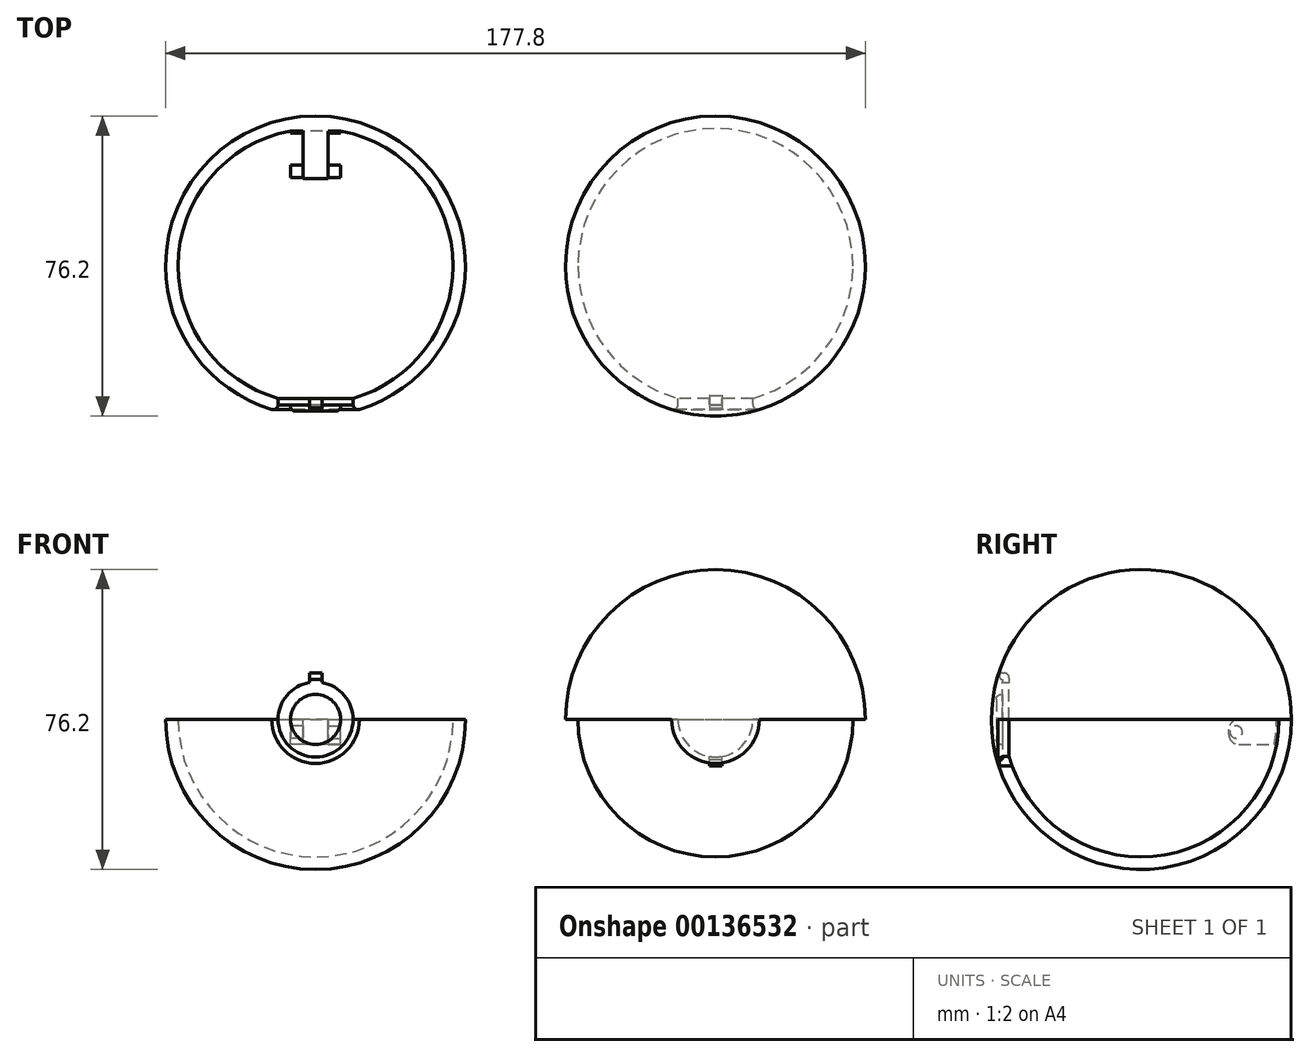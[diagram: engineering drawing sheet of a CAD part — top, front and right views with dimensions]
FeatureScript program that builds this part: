
annotation { "Feature Type Name" : "Feature", "Feature Type Description" : "" }
export const myFeature = defineFeature(function(context is Context, id is Id, definition is map)
    precondition{}
    {
        {
            var Q0;
            Q0=qCreatedBy(makeId("Top.planeOp"),FACE);
            var sketch = newSketch(context, id + "F0", { "sketchPlane" : qUnion([Q0])});
            skLineSegment(sketch, "E0", {"start": v(0, 0) * mm, "end": v(-50.8, 0) * mm});
            skCircle(sketch, "E1", {"center": v(-50.8, 0) * mm, "radius": 38.1 * mm});
            skLineSegment(sketch, "E2", {"start": v(0, 0) * mm, "end": v(50.8, 0) * mm});
            skCircle(sketch, "E3", {"center": v(50.8, 0) * mm, "radius": 38.1 * mm});
            skLineSegment(sketch, "E4", {"start": v(-50.8, 0) * mm, "end": v(-88.9, 0) * mm});
            skLineSegment(sketch, "E5", {"start": v(50.8, 0) * mm, "end": v(88.9, 0) * mm});
            skSolve(sketch);
        }
        {
            var Q0;
            {var subQ3=sQuery(id+"F0.wireOp",EDGE,"E4");Q0=makeQuery(id+"F0.imprint","IMPRINT",FACE,{"disambiguationData":[TD([[makeQuery(id+"F0.imprint","IMPRINT",EDGE,{"derivedFrom":subQ3}),1.0]])]});}
            var Q1;
            {var subQ3=sQuery(id+"F0.wireOp",EDGE,"E5");Q1=makeQuery(id+"F0.imprint","IMPRINT",FACE,{"disambiguationData":[TD([[makeQuery(id+"F0.imprint","IMPRINT",EDGE,{"derivedFrom":subQ3}),-1.0]])]});}
            var Q2;
            Q2=sQuery(id+"F0.wireOp",EDGE,"E0");
            revolve(context, id + "F1", {"surfaceOperationType" : NewSurfaceOperationType.NEW, "entities" : qUnion([Q0, Q1]), "axis" : qUnion([Q2]), "revolveType" : RevolveType.ONE_DIRECTION, "oppositeDirection" : true, "angle" : 180 * degree});
        }
        {
            var Q0;
            Q0=makeQuery(id+"F1.opRevolve","CAP_FACE",FACE,{"disambiguationData":[OSD([sQuery(id+"F0.wireOp",EDGE,"E0"),sQuery(id+"F0.wireOp",EDGE,"E1"),sQuery(id+"F0.wireOp",EDGE,"E4")])],"isStart":false});
            var sketch = newSketch(context, id + "F2", { "sketchPlane" : qUnion([Q0])});
            skCircle(sketch, "E6", {"center": v(-50.8, 0) * mm, "radius": 34.93 * mm});
            skLineSegment(sketch, "E7", {"start": v(-15.88, 0) * mm, "end": v(-85.73, 0) * mm});
            skSolve(sketch);
        }
        {
            var Q0;
            {var subQ0=sQuery(id+"F2.wireOp",EDGE,"E7");Q0=makeQuery(id+"F2.imprint","IMPRINT",FACE,{"disambiguationData":[TD([[makeQuery(id+"F2.imprint","IMPRINT",EDGE,{"derivedFrom":subQ0}),1.0]])]});}
            var Q1;
            Q1=sQuery(id+"F2.wireOp",EDGE,"E7");
            revolve(context, id + "F3", {"operationType" : NewBodyOperationType.REMOVE, "surfaceOperationType" : NewSurfaceOperationType.NEW, "entities" : qUnion([Q0]), "axis" : qUnion([Q1]), "revolveType" : RevolveType.FULL, "oppositeDirection" : true});
        }
        {
            var Q0;
            Q0=makeQuery(id+"F1.opRevolve","CAP_FACE",FACE,{"disambiguationData":[OSD([sQuery(id+"F0.wireOp",EDGE,"E2"),sQuery(id+"F0.wireOp",EDGE,"E3"),sQuery(id+"F0.wireOp",EDGE,"E5")])],"isStart":false});
            var sketch = newSketch(context, id + "F4", { "sketchPlane" : qUnion([Q0])});
            skCircle(sketch, "E8", {"center": v(50.8, 0) * mm, "radius": 34.93 * mm});
            skLineSegment(sketch, "E9", {"start": v(15.88, 0) * mm, "end": v(85.73, 0) * mm});
            skSolve(sketch);
        }
        {
            var Q0;
            {var subQ0=sQuery(id+"F4.wireOp",EDGE,"E9");Q0=makeQuery(id+"F4.imprint","IMPRINT",FACE,{"disambiguationData":[TD([[makeQuery(id+"F4.imprint","IMPRINT",EDGE,{"derivedFrom":subQ0}),-1.0]])]});}
            var Q1;
            Q1=sQuery(id+"F4.wireOp",EDGE,"E9");
            revolve(context, id + "F5", {"operationType" : NewBodyOperationType.REMOVE, "surfaceOperationType" : NewSurfaceOperationType.NEW, "entities" : qUnion([Q0]), "axis" : qUnion([Q1]), "revolveType" : RevolveType.FULL, "oppositeDirection" : true});
        }
        {
            var Q0;
            Q0=qCreatedBy(makeId("Front.planeOp"),FACE);
            var sketch = newSketch(context, id + "F6", { "sketchPlane" : qUnion([Q0])});
            skLineSegment(sketch, "E10", {"start": v(0, 0) * mm, "end": v(-50.8, 0) * mm});
            skCircle(sketch, "E11", {"center": v(-50.8, 0) * mm, "radius": 9.53 * mm});
            skSolve(sketch);
        }
        {
            var Q0;
            Q0 = qSketchRegion(id + "F6", true);
            extrude(context, id + "F7", {"entities" : qUnion([Q0]), "operationType" : NewBodyOperationType.REMOVE, "depth" : 50.8 * mm, "offsetDistance" : 25.4 * mm});
        }
        {
            var Q0;
            Q0=makeQuery(id+"F1.opRevolve","CAP_FACE",FACE,{"disambiguationData":[OSD([sQuery(id+"F0.wireOp",EDGE,"E0"),sQuery(id+"F0.wireOp",EDGE,"E1"),sQuery(id+"F0.wireOp",EDGE,"E4")])],"isStart":false});
            var sketch = newSketch(context, id + "F8", { "sketchPlane" : qUnion([Q0])});
            skLineSegment(sketch, "E12", {"start": v(-60.32, -33.6) * mm, "end": v(-41.28, -33.6) * mm});
            skLineSegment(sketch, "E13", {"start": v(-41.28, -33.6) * mm, "end": v(-41.28, -36.9) * mm});
            skLineSegment(sketch, "E14", {"start": v(-41.28, -36.9) * mm, "end": v(-60.33, -36.9) * mm});
            skLineSegment(sketch, "E15", {"start": v(-60.33, -36.9) * mm, "end": v(-60.33, -33.6) * mm});
            skLineSegment(sketch, "E16", {"start": v(-60.33, -33.6) * mm, "end": v(-60.33, -35.25) * mm});
            skLineSegment(sketch, "E17", {"start": v(-60.33, -35.25) * mm, "end": v(-41.28, -35.25) * mm});
            skLineSegment(sketch, "E18", {"start": v(-50.8, -33.6) * mm, "end": v(-50.8, -36.9) * mm});
            skLineSegment(sketch, "E19", {"start": v(-60.33, -35.25) * mm, "end": v(-57.15, -35.25) * mm});
            skLineSegment(sketch, "E20", {"start": v(-57.15, -35.25) * mm, "end": v(-57.15, -36.9) * mm});
            skSolve(sketch);
        }
        {
            var Q0;
            {var subQ0=sQuery(id+"F8.wireOp",EDGE,"E18");var subQ1=sQuery(id+"F8.wireOp",EDGE,"E17");var subQ2=makeQuery(id+"F8.imprint","INTERSECT",VERTEX,{"derivedFrom":[subQ1,subQ0]});Q0=makeQuery(id+"F8.imprint","IMPRINT",FACE,{"disambiguationData":[TD([[makeQuery(id+"F8.imprint","IMPRINT",EDGE,{"disambiguationData":[TD([[subQ2,1.0]])],"derivedFrom":subQ1}),1.0]])]});}
            var Q1;
            {var subQ3=sQuery(id+"F8.wireOp",EDGE,"E20");Q1=makeQuery(id+"F8.imprint","IMPRINT",FACE,{"disambiguationData":[TD([[makeQuery(id+"F8.imprint","IMPRINT",EDGE,{"derivedFrom":subQ3}),1.0]])]});}
            var Q2;
            Q2=sQuery(id+"F8.wireOp",EDGE,"E18");
            revolve(context, id + "F9", {"operationType" : NewBodyOperationType.ADD, "surfaceOperationType" : NewSurfaceOperationType.NEW, "entities" : qUnion([Q0, Q1]), "axis" : qUnion([Q2]), "revolveType" : RevolveType.FULL});
        }
        {
            var Q0;
            Q0=qCreatedBy(makeId("Front.planeOp"),FACE);
            var sketch = newSketch(context, id + "F10", { "sketchPlane" : qUnion([Q0])});
            skLineSegment(sketch, "E21", {"start": v(0, 0) * mm, "end": v(50.8, 0) * mm});
            skCircle(sketch, "E22", {"center": v(50.8, 0) * mm, "radius": 9.53 * mm});
            skSolve(sketch);
        }
        {
            var Q0;
            Q0 = qSketchRegion(id + "F10", true);
            extrude(context, id + "F11", {"entities" : qUnion([Q0]), "operationType" : NewBodyOperationType.REMOVE, "depth" : 50.8 * mm, "offsetDistance" : 25.4 * mm});
        }
        {
            var Q0;
            Q0=makeQuery(id+"F9.opRevolve","SWEPT_EDGE",EDGE,{"disambiguationData":[OSD([sQuery(id+"F8.wireOp",EDGE,"E14"),sQuery(id+"F8.wireOp",EDGE,"E20")])]});
            var Q1;
            Q1=makeQuery(id+"F7.boolean.opBoolean","INTERSECT",EDGE,{"derivedFrom":[makeQuery(id+"F1.opRevolve","SWEPT_FACE",FACE,{"disambiguationData":[OSD([sQuery(id+"F0.wireOp",EDGE,"E1")])]}),makeQuery(id+"F7.opExtrude","SWEPT_FACE",FACE,{"disambiguationData":[OSD([sQuery(id+"F6.wireOp",EDGE,"E11")])]})]});
            var Q2;
            Q2=makeQuery(id+"F11.boolean.opBoolean","INTERSECT",EDGE,{"derivedFrom":[makeQuery(id+"F1.opRevolve","SWEPT_FACE",FACE,{"disambiguationData":[OSD([sQuery(id+"F0.wireOp",EDGE,"E3")])]}),makeQuery(id+"F11.opExtrude","SWEPT_FACE",FACE,{"disambiguationData":[OSD([sQuery(id+"F10.wireOp",EDGE,"E22")])]})]});
            fillet(context, id + "F12", {"entities" : qUnion([Q0, Q1, Q2]), "tangentPropagation" : true, "radius" : 1.27 * mm, "defaultsChanged" : false, "vertexSettings" : [], "allowEdgeOverflow" : false});
        }
        {
            var Q0;
            Q0=makeQuery(id+"F1.opRevolve","CAP_FACE",FACE,{"disambiguationData":[OSD([sQuery(id+"F0.wireOp",EDGE,"E2"),sQuery(id+"F0.wireOp",EDGE,"E3"),sQuery(id+"F0.wireOp",EDGE,"E5")])],"isStart":false});
            var sketch = newSketch(context, id + "F13", { "sketchPlane" : qUnion([Q0])});
            skLineSegment(sketch, "E23", {"start": v(60.32, -33.6) * mm, "end": v(41.28, -33.6) * mm});
            skLineSegment(sketch, "E24", {"start": v(50.8, -33.6) * mm, "end": v(52.39, -33.6) * mm});
            skLineSegment(sketch, "E25", {"start": v(50.8, -33.6) * mm, "end": v(49.21, -33.6) * mm});
            skLineSegment(sketch, "E26", {"start": v(52.39, -33.6) * mm, "end": v(52.39, -35.25) * mm});
            skLineSegment(sketch, "E27", {"start": v(49.21, -33.6) * mm, "end": v(49.21, -35.25) * mm});
            skLineSegment(sketch, "E28", {"start": v(50.8, -33.6) * mm, "end": v(50.8, -35.25) * mm});
            skLineSegment(sketch, "E29", {"start": v(50.8, -35.25) * mm, "end": v(52.39, -35.25) * mm});
            skLineSegment(sketch, "E30", {"start": v(50.8, -35.25) * mm, "end": v(49.21, -35.25) * mm});
            skLineSegment(sketch, "E31", {"start": v(52.39, -33.6) * mm, "end": v(52.39, -33.1) * mm});
            skLineSegment(sketch, "E32", {"start": v(52.39, -33.1) * mm, "end": v(49.21, -33.1) * mm});
            skLineSegment(sketch, "E33", {"start": v(49.21, -33.1) * mm, "end": v(49.21, -33.6) * mm});
            skSolve(sketch);
        }
        {
            var Q0;
            {var subQ2=sQuery(id+"F13.wireOp",EDGE,"E26");Q0=makeQuery(id+"F13.imprint","IMPRINT",FACE,{"disambiguationData":[TD([[makeQuery(id+"F13.imprint","IMPRINT",EDGE,{"derivedFrom":subQ2}),-1.0]])]});}
            var Q1;
            {var subQ0=sQuery(id+"F13.wireOp",EDGE,"E27");Q1=makeQuery(id+"F13.imprint","IMPRINT",FACE,{"disambiguationData":[TD([[makeQuery(id+"F13.imprint","IMPRINT",EDGE,{"derivedFrom":subQ0}),1.0]])]});}
            var Q2;
            {var subQ0=sQuery(id+"F13.wireOp",EDGE,"E31");Q2=makeQuery(id+"F13.imprint","IMPRINT",FACE,{"disambiguationData":[TD([[makeQuery(id+"F13.imprint","IMPRINT",EDGE,{"derivedFrom":subQ0}),1.0]])]});}
            extrude(context, id + "F14", {"entities" : qUnion([Q0, Q1, Q2]), "operationType" : NewBodyOperationType.REMOVE, "oppositeDirection" : true, "depth" : 10.16 * mm, "offsetDistance" : 25.4 * mm});
        }
        {
            var Q0;
            Q0=makeQuery(id+"F9.opRevolve","SWEPT_FACE",FACE,{"disambiguationData":[OSD([sQuery(id+"F8.wireOp",EDGE,"E12")])]});
            var sketch = newSketch(context, id + "F15", { "sketchPlane" : qUnion([Q0])});
            skLineSegment(sketch, "E34", {"start": v(50.8, 0) * mm, "end": v(50.8, 9.52) * mm});
            skLineSegment(sketch, "E35", {"start": v(50.8, 9.52) * mm, "end": v(52.39, 9.52) * mm});
            skLineSegment(sketch, "E36", {"start": v(50.8, 9.52) * mm, "end": v(49.21, 9.52) * mm});
            skLineSegment(sketch, "E37", {"start": v(49.21, 9.52) * mm, "end": v(49.21, 9.4) * mm});
            skLineSegment(sketch, "E38", {"start": v(52.39, 9.52) * mm, "end": v(52.39, 9.4) * mm});
            skSolve(sketch);
        }
        {
            var Q0;
            Q0 = qSketchRegion(id + "F15", true);
            var Q1;
            {var subQ0=sQuery(id+"F15.wireOp",EDGE,"E36");Q1=makeQuery(id+"F15.imprint","IMPRINT",FACE,{"disambiguationData":[TD([[makeQuery(id+"F15.imprint","IMPRINT",EDGE,{"derivedFrom":subQ0}),1.0]])]});}
            var Q2;
            {var subQ0=sQuery(id+"F15.wireOp",EDGE,"E35");Q2=makeQuery(id+"F15.imprint","IMPRINT",FACE,{"disambiguationData":[TD([[makeQuery(id+"F15.imprint","IMPRINT",EDGE,{"derivedFrom":subQ0}),-1.0]])]});}
            extrude(context, id + "F16", {"entities" : qUnion([Q0, Q1, Q2]), "operationType" : NewBodyOperationType.ADD, "oppositeDirection" : true, "depth" : 1.65 * mm, "offsetDistance" : 25.4 * mm});
        }
        {
            var Q0;
            Q0=makeQuery(id+"F16.boolean.opBoolean","MERGE",FACE,{"derivedFrom":[makeQuery(id+"F16.opExtrude","SWEPT_FACE",FACE,{"disambiguationData":[OSD([sQuery(id+"F15.wireOp",EDGE,"E35")])]}),makeQuery(id+"F16.opExtrude","SWEPT_FACE",FACE,{"disambiguationData":[OSD([sQuery(id+"F15.wireOp",EDGE,"E36")])]})]});
            extrude(context, id + "F17", {"entities" : qUnion([Q0]), "operationType" : NewBodyOperationType.ADD, "depth" : 0.64 * mm, "offsetDistance" : 25.4 * mm});
        }
        {
            var Q0;
            Q0=makeQuery(id+"F17.opExtrude","CAP_FACE",FACE,{"disambiguationData":[OSD([sQuery(id+"F15.wireOp",EDGE,"E35"),sQuery(id+"F15.wireOp",EDGE,"E36")])],"isStart":false});
            extrude(context, id + "F18", {"entities" : qUnion([Q0]), "operationType" : NewBodyOperationType.ADD, "depth" : 1.65 * mm, "offsetDistance" : 25.4 * mm});
        }
        {
            var Q0;
            {var subQ0=sQuery(id+"F15.wireOp",EDGE,"E37");var subQ1=sQuery(id+"F15.wireOp",EDGE,"E36");Q0=makeQuery(id+"F18.boolean.opBoolean","MERGE",FACE,{"derivedFrom":[makeQuery(id+"F17.boolean.opBoolean","MERGE",FACE,{"derivedFrom":[makeQuery(id+"F16.opExtrude","SWEPT_FACE",FACE,{"disambiguationData":[OSD([subQ0])]}),makeQuery(id+"F17.opExtrude","SWEPT_FACE",FACE,{"disambiguationData":[OSD([subQ1,subQ0])]})]}),makeQuery(id+"F18.opExtrude","SWEPT_FACE",FACE,{"disambiguationData":[OSD([subQ1,subQ0])]})]});}
            var sketch = newSketch(context, id + "F19", { "sketchPlane" : qUnion([Q0])});
            skCircle(sketch, "E39", {"center": v(-35.25, 10.99) * mm, "radius": 0.83 * mm});
            skLineSegment(sketch, "E40", {"start": v(-35.25, 10.16) * mm, "end": v(-35.25, 11.81) * mm});
            skSolve(sketch);
        }
        {
            var Q0;
            Q0 = qSketchRegion(id + "F19", true);
            extrude(context, id + "F20", {"entities" : qUnion([Q0]), "operationType" : NewBodyOperationType.ADD, "oppositeDirection" : true, "depth" : 3.17 * mm, "offsetDistance" : 25.4 * mm});
        }
        {
            var Q0;
            {var subQ0=sQuery(id+"F15.wireOp",EDGE,"E36");var subQ1=sQuery(id+"F15.wireOp",EDGE,"E35");Q0=makeQuery(id+"F18.opExtrude","CAP_EDGE",EDGE,{"disambiguationData":[OSD([subQ1,subQ0]),TDD([makeQuery(id+"F17.opExtrude","CAP_EDGE",EDGE,{"disambiguationData":[OSD([subQ1,subQ0]),TDD([makeQuery(id+"F16.boolean.opBoolean","MERGE",EDGE,{"derivedFrom":[makeQuery(id+"F16.opExtrude","CAP_EDGE",EDGE,{"disambiguationData":[OSD([subQ1])],"isStart":true}),makeQuery(id+"F16.opExtrude","CAP_EDGE",EDGE,{"disambiguationData":[OSD([subQ0])],"isStart":true})]})])],"isStart":false})])],"isStart":false});}
            fillet(context, id + "F21", {"entities" : qUnion([Q0]), "tangentPropagation" : true, "radius" : 1.27 * mm, "defaultsChanged" : true, "vertexSettings" : [], "allowEdgeOverflow" : false});
        }
        {
            var Q0;
            Q0=makeQuery(id+"F14.boolean.opBoolean","COPY",FACE,{"derivedFrom":makeQuery(id+"F14.opExtrude","CAP_FACE",FACE,{"disambiguationData":[OSD([sQuery(id+"F13.wireOp",EDGE,"E26"),sQuery(id+"F13.wireOp",EDGE,"E27"),sQuery(id+"F13.wireOp",EDGE,"E29"),sQuery(id+"F13.wireOp",EDGE,"E30"),sQuery(id+"F13.wireOp",EDGE,"E31"),sQuery(id+"F13.wireOp",EDGE,"E32"),sQuery(id+"F13.wireOp",EDGE,"E33")])],"isStart":false})});
            var sketch = newSketch(context, id + "F22", { "sketchPlane" : qUnion([Q0])});
            skLineSegment(sketch, "E41.bottom", {"start": v(52.39, -35.25) * mm, "end": v(49.21, -35.25) * mm});
            skLineSegment(sketch, "E41.top", {"start": v(52.39, -32.08) * mm, "end": v(49.21, -32.08) * mm});
            skLineSegment(sketch, "E41.left", {"start": v(52.39, -35.25) * mm, "end": v(52.39, -32.08) * mm});
            skLineSegment(sketch, "E41.right", {"start": v(49.21, -35.25) * mm, "end": v(49.21, -32.08) * mm});
            skSolve(sketch);
        }
        {
            var Q0;
            Q0 = qSketchRegion(id + "F22", true);
            extrude(context, id + "F23", {"entities" : qUnion([Q0]), "operationType" : NewBodyOperationType.REMOVE, "oppositeDirection" : true, "depth" : 1.65 * mm, "offsetDistance" : 25.4 * mm});
        }
        {
            var Q0;
            Q0=makeQuery(id+"F23.boolean.opBoolean","MERGE",FACE,{"derivedFrom":[makeQuery(id+"F14.boolean.opBoolean","COPY",FACE,{"derivedFrom":makeQuery(id+"F14.opExtrude","SWEPT_FACE",FACE,{"disambiguationData":[OSD([sQuery(id+"F13.wireOp",EDGE,"E26"),sQuery(id+"F13.wireOp",EDGE,"E31")])]})})],"fromTools":[makeQuery(id+"F23.opExtrude","SWEPT_FACE",FACE,{"disambiguationData":[OSD([sQuery(id+"F22.wireOp",EDGE,"E41.left")])]})]});
            var sketch = newSketch(context, id + "F24", { "sketchPlane" : qUnion([Q0])});
            skCircle(sketch, "E42", {"center": v(35.25, -10.99) * mm, "radius": 0.83 * mm});
            skSolve(sketch);
        }
        {
            var Q0;
            Q0 = qSketchRegion(id + "F24", true);
            extrude(context, id + "F25", {"entities" : qUnion([Q0]), "operationType" : NewBodyOperationType.REMOVE, "depth" : 3.17 * mm, "offsetDistance" : 25.4 * mm});
        }
        {
            var Q0;
            Q0=makeQuery(id+"F1.opRevolve","CAP_FACE",FACE,{"disambiguationData":[OSD([sQuery(id+"F0.wireOp",EDGE,"E0"),sQuery(id+"F0.wireOp",EDGE,"E1"),sQuery(id+"F0.wireOp",EDGE,"E4")])],"isStart":false});
            var sketch = newSketch(context, id + "F26", { "sketchPlane" : qUnion([Q0])});
            skLineSegment(sketch, "E43", {"start": v(-50.8, 34.92) * mm, "end": v(-50.8, 22.23) * mm});
            skLineSegment(sketch, "E44", {"start": v(-50.8, 22.23) * mm, "end": v(-57.15, 22.23) * mm});
            skLineSegment(sketch, "E45", {"start": v(-57.15, 22.23) * mm, "end": v(-57.15, 34.34) * mm});
            skLineSegment(sketch, "E46.MirrorCS", {"start": v(-44.45, 22.23) * mm, "end": v(-44.45, 34.34) * mm});
            skLineSegment(sketch, "E47.MirrorCS", {"start": v(-50.8, 22.23) * mm, "end": v(-44.45, 22.23) * mm});
            skSolve(sketch);
        }
        {
            var Q0;
            {var subQ0=sQuery(id+"F26.wireOp",EDGE,"E43");Q0=makeQuery(id+"F26.imprint","IMPRINT",FACE,{"disambiguationData":[TD([[makeQuery(id+"F26.imprint","IMPRINT",EDGE,{"derivedFrom":subQ0}),-1.0]])]});}
            var Q1;
            {var subQ0=sQuery(id+"F26.wireOp",EDGE,"E43");Q1=makeQuery(id+"F26.imprint","IMPRINT",FACE,{"disambiguationData":[TD([[makeQuery(id+"F26.imprint","IMPRINT",EDGE,{"derivedFrom":subQ0}),1.0]])]});}
            extrude(context, id + "F27", {"entities" : qUnion([Q0, Q1]), "operationType" : NewBodyOperationType.ADD, "oppositeDirection" : true, "depth" : 6.35 * mm, "offsetDistance" : 25.4 * mm});
        }
        {
            var Q0;
            Q0=makeQuery(id+"F27.opExtrude","SWEPT_FACE",FACE,{"disambiguationData":[OSD([sQuery(id+"F26.wireOp",EDGE,"E45")])]});
            var sketch = newSketch(context, id + "F28", { "sketchPlane" : qUnion([Q0])});
            skPoint(sketch, "E48.centerSnap0", {"position": v(-20.87, -3.18) * mm});
            skCircle(sketch, "E49", {"center": v(-24.07, -3.18) * mm, "radius": 1.59 * mm});
            skPoint(sketch, "E49.centerSnap0", {"position": v(-22.23, -3.18) * mm});
            skLineSegment(sketch, "E50", {"start": v(-22.48, -3.18) * mm, "end": v(-22.23, -3.18) * mm});
            skSolve(sketch);
        }
        {
            var Q0;
            Q0=makeQuery(id+"F28.imprint","IMPRINT",FACE,{"disambiguationData":[TD([[makeQuery(id+"F28.imprint","IMPRINT",EDGE,{"derivedFrom":sQuery(id+"F28.wireOp",EDGE,"E49")}),-1.0]])]});
            extrude(context, id + "F29", {"entities" : qUnion([Q0]), "operationType" : NewBodyOperationType.REMOVE, "oppositeDirection" : true, "depth" : 3.17 * mm, "offsetDistance" : 25.4 * mm});
        }
        {
            var Q0;
            Q0=makeQuery(id+"F27.opExtrude","SWEPT_FACE",FACE,{"disambiguationData":[OSD([sQuery(id+"F26.wireOp",EDGE,"E46.MirrorCS")])]});
            var sketch = newSketch(context, id + "F30", { "sketchPlane" : qUnion([Q0])});
            skCircle(sketch, "E51", {"center": v(24.07, -3.18) * mm, "radius": 1.59 * mm});
            skPoint(sketch, "E51.centerSnap0", {"position": v(22.23, -3.18) * mm});
            skLineSegment(sketch, "E52", {"start": v(22.23, -3.18) * mm, "end": v(22.48, -3.18) * mm});
            skSolve(sketch);
        }
        {
            var Q0;
            Q0=makeQuery(id+"F30.imprint","IMPRINT",FACE,{"disambiguationData":[TD([[makeQuery(id+"F30.imprint","IMPRINT",EDGE,{"derivedFrom":sQuery(id+"F30.wireOp",EDGE,"E51")}),-1.0]])]});
            extrude(context, id + "F31", {"entities" : qUnion([Q0]), "operationType" : NewBodyOperationType.REMOVE, "oppositeDirection" : true, "depth" : 3.17 * mm, "offsetDistance" : 25.4 * mm});
        }
        {
            var Q0;
            Q0=makeQuery(id+"F27.opExtrude","CAP_EDGE",EDGE,{"disambiguationData":[OSD([sQuery(id+"F26.wireOp",EDGE,"E44"),sQuery(id+"F26.wireOp",EDGE,"E47.MirrorCS")])],"isStart":true});
            var Q1;
            Q1=makeQuery(id+"F27.opExtrude","CAP_EDGE",EDGE,{"disambiguationData":[OSD([sQuery(id+"F26.wireOp",EDGE,"E44"),sQuery(id+"F26.wireOp",EDGE,"E47.MirrorCS")])],"isStart":false});
            fillet(context, id + "F32", {"entities" : qUnion([Q0, Q1]), "tangentPropagation" : true, "radius" : 2.54 * mm, "defaultsChanged" : true, "vertexSettings" : [], "allowEdgeOverflow" : false});
        }
    });
